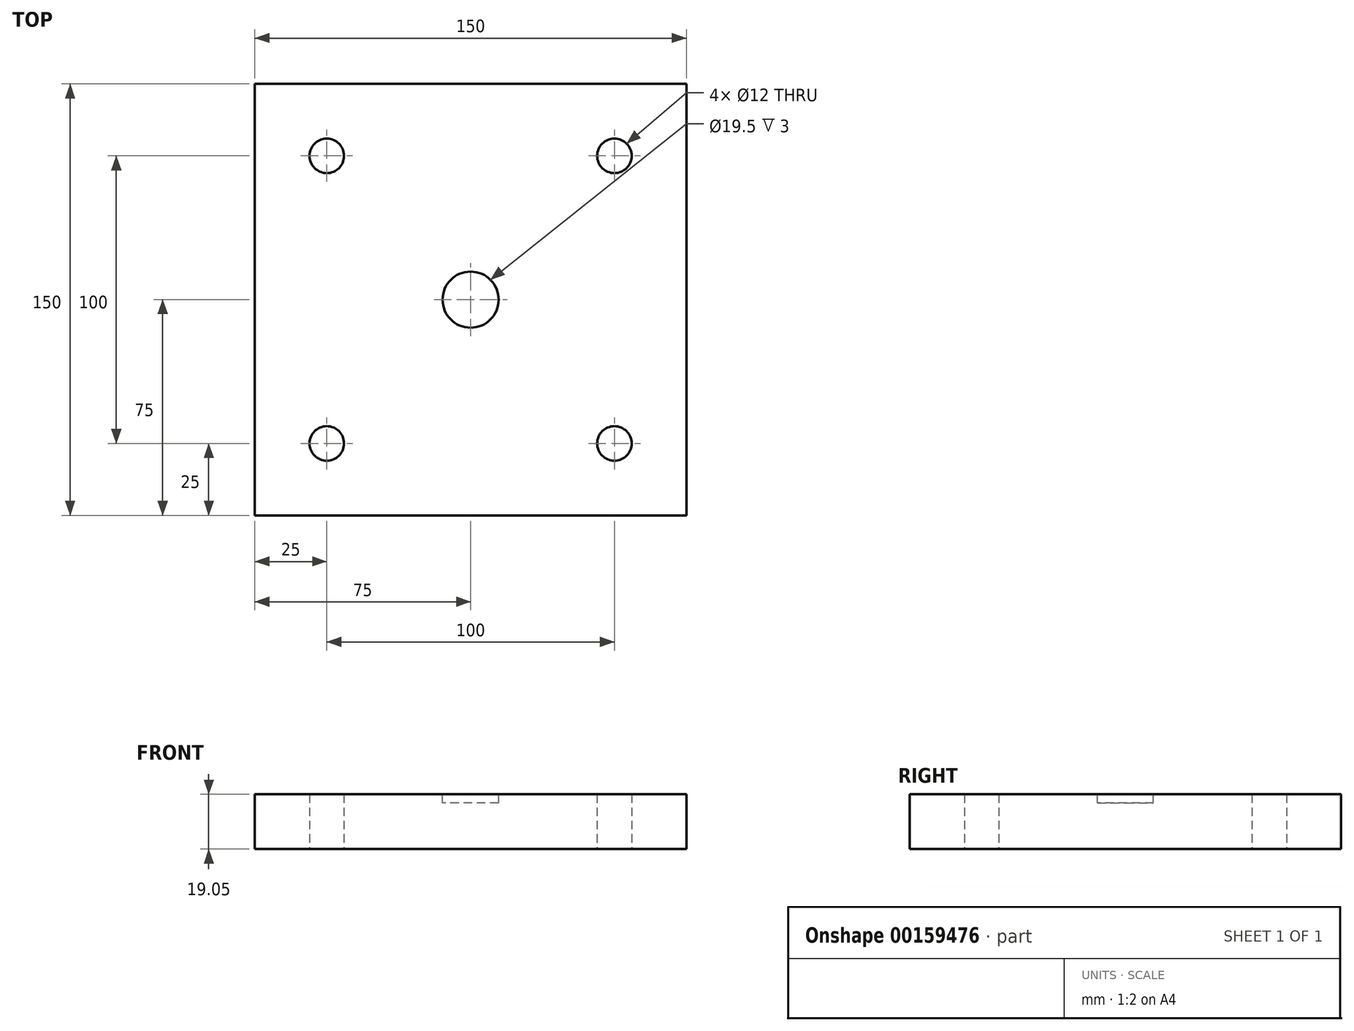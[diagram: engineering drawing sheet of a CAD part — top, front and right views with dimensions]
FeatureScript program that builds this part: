
annotation { "Feature Type Name" : "Feature", "Feature Type Description" : "" }
export const myFeature = defineFeature(function(context is Context, id is Id, definition is map)
    precondition{}
    {
        {
            var Q0;
            Q0=qCreatedBy(makeId("Top.planeOp"),FACE);
            var sketch = newSketch(context, id + "F0", { "sketchPlane" : qUnion([Q0])});
            skLineSegment(sketch, "E0.bottom", {"start": v(0, 0) * mm, "end": v(150, 0) * mm});
            skLineSegment(sketch, "E0.top", {"start": v(0, 150) * mm, "end": v(150, 150) * mm});
            skLineSegment(sketch, "E0.left", {"start": v(0, 0) * mm, "end": v(0, 150) * mm});
            skLineSegment(sketch, "E0.right", {"start": v(150, 0) * mm, "end": v(150, 150) * mm});
            skCircle(sketch, "E1", {"center": v(25, 125) * mm, "radius": 6 * mm});
            skCircle(sketch, "E2", {"center": v(125, 125) * mm, "radius": 6 * mm});
            skCircle(sketch, "E3", {"center": v(25, 25) * mm, "radius": 6 * mm});
            skCircle(sketch, "E4", {"center": v(125, 25) * mm, "radius": 6 * mm});
            skSolve(sketch);
        }
        {
            var Q0;
            Q0 = qSketchRegion(id + "F0", true);
            extrude(context, id + "F1", {"entities" : qUnion([Q0]), "depth" : 19.05 * mm});
        }
        {
            var Q0;
            Q0=makeQuery(id+"F1.opExtrude","CAP_FACE",FACE,{"disambiguationData":[OSD([sQuery(id+"F0.wireOp",EDGE,"E0.bottom"),sQuery(id+"F0.wireOp",EDGE,"E0.top"),sQuery(id+"F0.wireOp",EDGE,"E0.left"),sQuery(id+"F0.wireOp",EDGE,"E0.right"),sQuery(id+"F0.wireOp",EDGE,"E1"),sQuery(id+"F0.wireOp",EDGE,"E2"),sQuery(id+"F0.wireOp",EDGE,"E3"),sQuery(id+"F0.wireOp",EDGE,"E4")])],"isStart":false});
            var sketch = newSketch(context, id + "F2", { "sketchPlane" : qUnion([Q0])});
            skCircle(sketch, "E5", {"center": v(75, 75) * mm, "radius": 9.75 * mm});
            skSolve(sketch);
        }
        {
            var Q0;
            Q0 = qSketchRegion(id + "F2", true);
            extrude(context, id + "F3", {"entities" : qUnion([Q0]), "operationType" : NewBodyOperationType.REMOVE, "oppositeDirection" : true, "depth" : 3 * mm});
        }
    });
